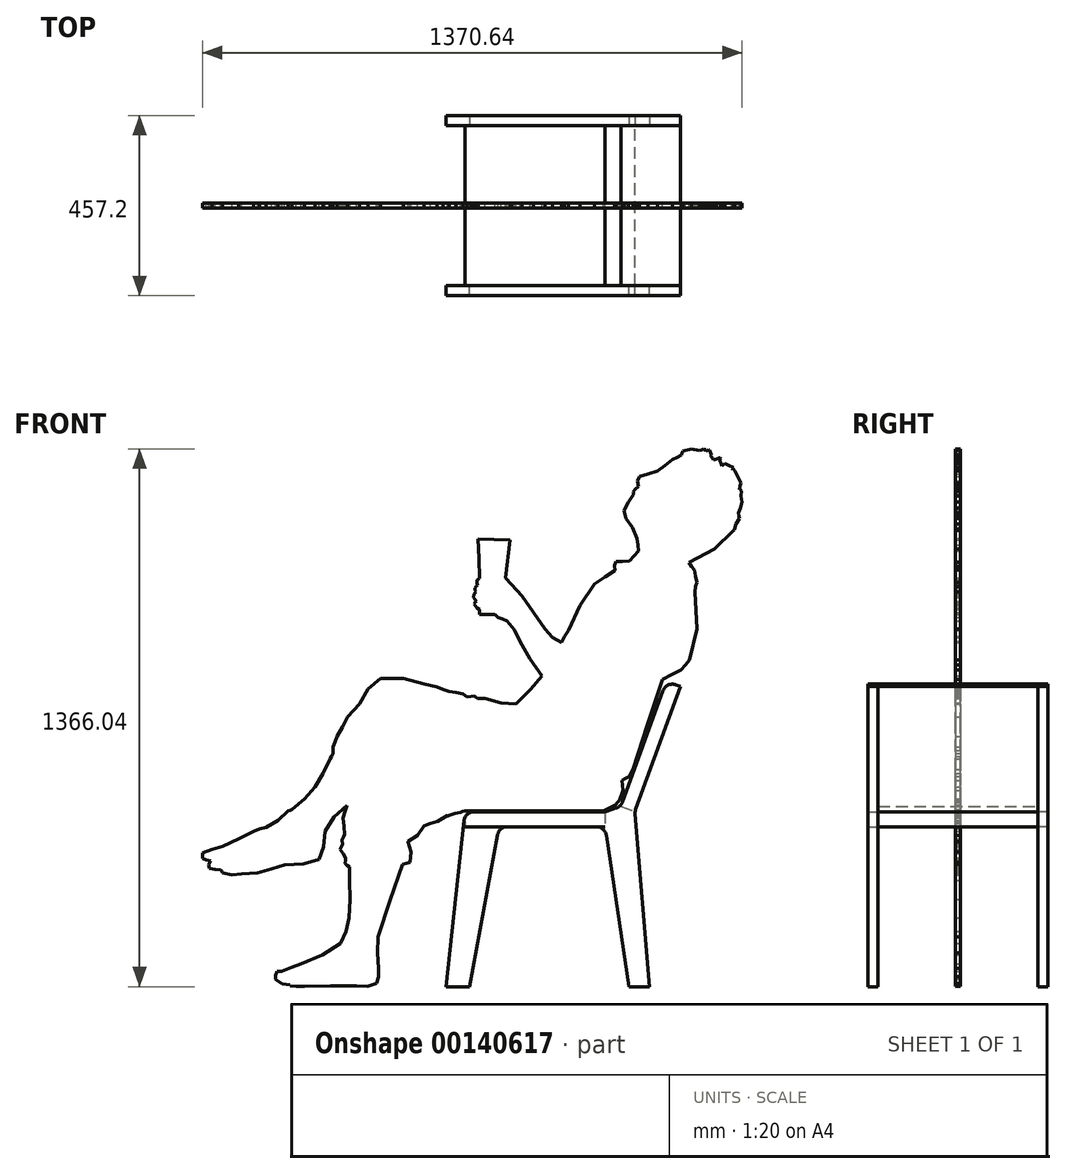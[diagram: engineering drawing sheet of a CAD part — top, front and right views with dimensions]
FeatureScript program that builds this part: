
annotation { "Feature Type Name" : "Feature", "Feature Type Description" : "" }
export const myFeature = defineFeature(function(context is Context, id is Id, definition is map)
    precondition{}
    {
        {
            var Q0;
            Q0=qCreatedBy(makeId("Front.planeOp"),FACE);
            var sketch = newSketch(context, id + "F0", { "sketchPlane" : qUnion([Q0])});
            skLineSegment(sketch, "E0", {"start": v(230.04, 462.13) * mm, "end": v(234.88, 467.85) * mm});
            skLineSegment(sketch, "E1", {"start": v(234.88, 467.85) * mm, "end": v(240.17, 473.23) * mm});
            skLineSegment(sketch, "E2", {"start": v(240.17, 473.23) * mm, "end": v(249.09, 499.16) * mm});
            skLineSegment(sketch, "E3", {"start": v(249.09, 499.16) * mm, "end": v(246.4, 524.65) * mm});
            skLineSegment(sketch, "E4", {"start": v(246.4, 524.65) * mm, "end": v(255.7, 529.38) * mm});
            skLineSegment(sketch, "E5", {"start": v(255.7, 529.38) * mm, "end": v(265.03, 534.12) * mm});
            skLineSegment(sketch, "E6", {"start": v(265.03, 534.12) * mm, "end": v(269.43, 542.97) * mm});
            skLineSegment(sketch, "E7", {"start": v(269.43, 542.97) * mm, "end": v(273.88, 551.78) * mm});
            skLineSegment(sketch, "E8", {"start": v(273.88, 551.78) * mm, "end": v(311.72, 666.33) * mm});
            skLineSegment(sketch, "E9", {"start": v(311.72, 666.33) * mm, "end": v(349.55, 780.89) * mm});
            skLineSegment(sketch, "E10", {"start": v(349.55, 780.89) * mm, "end": v(372.82, 793.09) * mm});
            skLineSegment(sketch, "E11", {"start": v(372.82, 793.09) * mm, "end": v(396.1, 805.28) * mm});
            skLineSegment(sketch, "E12", {"start": v(396.1, 805.28) * mm, "end": v(407.83, 817.46) * mm});
            skLineSegment(sketch, "E13", {"start": v(407.83, 817.46) * mm, "end": v(417.82, 830.69) * mm});
            skLineSegment(sketch, "E14", {"start": v(417.82, 830.69) * mm, "end": v(437.54, 908.46) * mm});
            skLineSegment(sketch, "E15", {"start": v(437.54, 908.46) * mm, "end": v(431.89, 1002.35) * mm});
            skLineSegment(sketch, "E16", {"start": v(431.89, 1002.35) * mm, "end": v(432.93, 1016.38) * mm});
            skLineSegment(sketch, "E17", {"start": v(432.93, 1016.38) * mm, "end": v(436.5, 1027.04) * mm});
            skLineSegment(sketch, "E18", {"start": v(436.5, 1027.04) * mm, "end": v(433.6, 1043) * mm});
            skLineSegment(sketch, "E19", {"start": v(433.6, 1043) * mm, "end": v(430.68, 1058.92) * mm});
            skLineSegment(sketch, "E20", {"start": v(430.68, 1058.92) * mm, "end": v(423.59, 1067.86) * mm});
            skLineSegment(sketch, "E21", {"start": v(423.59, 1067.86) * mm, "end": v(416.63, 1078.02) * mm});
            skLineSegment(sketch, "E22", {"start": v(416.63, 1078.02) * mm, "end": v(480.94, 1111.8) * mm});
            skLineSegment(sketch, "E23", {"start": v(480.94, 1111.8) * mm, "end": v(529.37, 1159.29) * mm});
            skLineSegment(sketch, "E24", {"start": v(529.37, 1159.29) * mm, "end": v(531.82, 1160.03) * mm});
            skLineSegment(sketch, "E25", {"start": v(531.82, 1160.03) * mm, "end": v(532.62, 1161.32) * mm});
            skLineSegment(sketch, "E26", {"start": v(532.62, 1161.32) * mm, "end": v(536.36, 1175.51) * mm});
            skLineSegment(sketch, "E27", {"start": v(536.36, 1175.51) * mm, "end": v(544.96, 1188.92) * mm});
            skLineSegment(sketch, "E28", {"start": v(544.96, 1188.92) * mm, "end": v(543.9, 1196.32) * mm});
            skLineSegment(sketch, "E29", {"start": v(543.9, 1196.32) * mm, "end": v(542.61, 1203.61) * mm});
            skLineSegment(sketch, "E30", {"start": v(542.61, 1203.61) * mm, "end": v(548.02, 1216.63) * mm});
            skLineSegment(sketch, "E31", {"start": v(548.02, 1216.63) * mm, "end": v(551.7, 1230.97) * mm});
            skLineSegment(sketch, "E32", {"start": v(551.7, 1230.97) * mm, "end": v(548.93, 1246.33) * mm});
            skLineSegment(sketch, "E33", {"start": v(548.93, 1246.33) * mm, "end": v(550.4, 1259.92) * mm});
            skLineSegment(sketch, "E34", {"start": v(550.4, 1259.92) * mm, "end": v(548.03, 1262.67) * mm});
            skLineSegment(sketch, "E35", {"start": v(548.03, 1262.67) * mm, "end": v(544.89, 1263.55) * mm});
            skLineSegment(sketch, "E36", {"start": v(544.89, 1263.55) * mm, "end": v(546.36, 1272.14) * mm});
            skLineSegment(sketch, "E37", {"start": v(546.36, 1272.14) * mm, "end": v(548.52, 1279.69) * mm});
            skLineSegment(sketch, "E38", {"start": v(548.52, 1279.69) * mm, "end": v(541.03, 1294.78) * mm});
            skLineSegment(sketch, "E39", {"start": v(541.03, 1294.78) * mm, "end": v(533.46, 1309.96) * mm});
            skLineSegment(sketch, "E40", {"start": v(533.46, 1309.96) * mm, "end": v(529.26, 1314.78) * mm});
            skLineSegment(sketch, "E41", {"start": v(529.26, 1314.78) * mm, "end": v(524.28, 1317.05) * mm});
            skLineSegment(sketch, "E42", {"start": v(524.28, 1317.05) * mm, "end": v(526.76, 1318) * mm});
            skLineSegment(sketch, "E43", {"start": v(526.76, 1318) * mm, "end": v(529.24, 1318.96) * mm});
            skLineSegment(sketch, "E44", {"start": v(529.24, 1318.96) * mm, "end": v(518.3, 1324.37) * mm});
            skLineSegment(sketch, "E45", {"start": v(518.3, 1324.37) * mm, "end": v(507.96, 1329.59) * mm});
            skLineSegment(sketch, "E46", {"start": v(507.96, 1329.59) * mm, "end": v(504.43, 1326.13) * mm});
            skLineSegment(sketch, "E47", {"start": v(504.43, 1326.13) * mm, "end": v(500.73, 1322.78) * mm});
            skLineSegment(sketch, "E48", {"start": v(500.73, 1322.78) * mm, "end": v(498.52, 1330.1) * mm});
            skLineSegment(sketch, "E49", {"start": v(498.52, 1330.1) * mm, "end": v(495.12, 1335.27) * mm});
            skLineSegment(sketch, "E50", {"start": v(495.12, 1335.27) * mm, "end": v(495.7, 1339.01) * mm});
            skLineSegment(sketch, "E51", {"start": v(495.7, 1339.01) * mm, "end": v(497.46, 1341.92) * mm});
            skLineSegment(sketch, "E52", {"start": v(497.46, 1341.92) * mm, "end": v(496.73, 1342.9) * mm});
            skLineSegment(sketch, "E53", {"start": v(496.73, 1342.9) * mm, "end": v(496.02, 1343.81) * mm});
            skLineSegment(sketch, "E54", {"start": v(496.02, 1343.81) * mm, "end": v(485.87, 1340.85) * mm});
            skLineSegment(sketch, "E55", {"start": v(485.87, 1340.85) * mm, "end": v(478.3, 1338.56) * mm});
            skLineSegment(sketch, "E56", {"start": v(478.3, 1338.56) * mm, "end": v(476.02, 1343.16) * mm});
            skLineSegment(sketch, "E57", {"start": v(476.02, 1343.16) * mm, "end": v(472.6, 1347.16) * mm});
            skLineSegment(sketch, "E58", {"start": v(472.6, 1347.16) * mm, "end": v(472.25, 1349.6) * mm});
            skLineSegment(sketch, "E59", {"start": v(472.25, 1349.6) * mm, "end": v(474.32, 1351.05) * mm});
            skLineSegment(sketch, "E60", {"start": v(474.32, 1351.05) * mm, "end": v(471.62, 1356.97) * mm});
            skLineSegment(sketch, "E61", {"start": v(471.62, 1356.97) * mm, "end": v(468.92, 1362.9) * mm});
            skLineSegment(sketch, "E62", {"start": v(468.92, 1362.9) * mm, "end": v(467.81, 1363.7) * mm});
            skLineSegment(sketch, "E63", {"start": v(467.81, 1363.7) * mm, "end": v(466.71, 1364.49) * mm});
            skLineSegment(sketch, "E64", {"start": v(466.71, 1364.49) * mm, "end": v(463.44, 1362.38) * mm});
            skLineSegment(sketch, "E65", {"start": v(463.44, 1362.38) * mm, "end": v(460.11, 1360.3) * mm});
            skLineSegment(sketch, "E66", {"start": v(460.11, 1360.3) * mm, "end": v(459.63, 1362.58) * mm});
            skLineSegment(sketch, "E67", {"start": v(459.63, 1362.58) * mm, "end": v(459.17, 1364.81) * mm});
            skLineSegment(sketch, "E68", {"start": v(459.17, 1364.81) * mm, "end": v(456.52, 1364.22) * mm});
            skLineSegment(sketch, "E69", {"start": v(456.52, 1364.22) * mm, "end": v(453.9, 1363.58) * mm});
            skLineSegment(sketch, "E70", {"start": v(453.9, 1363.58) * mm, "end": v(453.85, 1364.82) * mm});
            skLineSegment(sketch, "E71", {"start": v(453.85, 1364.82) * mm, "end": v(453.75, 1366.04) * mm});
            skLineSegment(sketch, "E72", {"start": v(453.75, 1366.04) * mm, "end": v(448.81, 1363.92) * mm});
            skLineSegment(sketch, "E73", {"start": v(448.81, 1363.92) * mm, "end": v(443.13, 1361.95) * mm});
            skLineSegment(sketch, "E74", {"start": v(443.13, 1361.95) * mm, "end": v(422.6, 1365.55) * mm});
            skLineSegment(sketch, "E75", {"start": v(422.6, 1365.55) * mm, "end": v(401.85, 1360.7) * mm});
            skLineSegment(sketch, "E76", {"start": v(401.85, 1360.7) * mm, "end": v(399.46, 1355.35) * mm});
            skLineSegment(sketch, "E77", {"start": v(399.46, 1355.35) * mm, "end": v(397.72, 1350.2) * mm});
            skLineSegment(sketch, "E78", {"start": v(397.72, 1350.2) * mm, "end": v(386.13, 1344.92) * mm});
            skLineSegment(sketch, "E79", {"start": v(386.13, 1344.92) * mm, "end": v(374.59, 1339.72) * mm});
            skLineSegment(sketch, "E80", {"start": v(374.59, 1339.72) * mm, "end": v(355.17, 1324.14) * mm});
            skLineSegment(sketch, "E81", {"start": v(355.17, 1324.14) * mm, "end": v(337.03, 1309.65) * mm});
            skLineSegment(sketch, "E82", {"start": v(337.03, 1309.65) * mm, "end": v(312.55, 1303.07) * mm});
            skLineSegment(sketch, "E83", {"start": v(312.55, 1303.07) * mm, "end": v(290.53, 1296.61) * mm});
            skLineSegment(sketch, "E84", {"start": v(290.53, 1296.61) * mm, "end": v(285.93, 1284.95) * mm});
            skLineSegment(sketch, "E85", {"start": v(285.93, 1284.95) * mm, "end": v(288.26, 1270.38) * mm});
            skLineSegment(sketch, "E86", {"start": v(288.26, 1270.38) * mm, "end": v(280.8, 1263.87) * mm});
            skLineSegment(sketch, "E87", {"start": v(280.8, 1263.87) * mm, "end": v(274.61, 1256.95) * mm});
            skLineSegment(sketch, "E88", {"start": v(274.61, 1256.95) * mm, "end": v(275.36, 1253.9) * mm});
            skLineSegment(sketch, "E89", {"start": v(275.36, 1253.9) * mm, "end": v(276.14, 1250.9) * mm});
            skLineSegment(sketch, "E90", {"start": v(276.14, 1250.9) * mm, "end": v(262.68, 1231.99) * mm});
            skLineSegment(sketch, "E91", {"start": v(262.68, 1231.99) * mm, "end": v(251.18, 1209.39) * mm});
            skLineSegment(sketch, "E92", {"start": v(251.18, 1209.39) * mm, "end": v(254.22, 1199.43) * mm});
            skLineSegment(sketch, "E93", {"start": v(254.22, 1199.43) * mm, "end": v(257.27, 1189.53) * mm});
            skLineSegment(sketch, "E94", {"start": v(257.27, 1189.53) * mm, "end": v(272.63, 1166.4) * mm});
            skLineSegment(sketch, "E95", {"start": v(272.63, 1166.4) * mm, "end": v(284.92, 1138.68) * mm});
            skLineSegment(sketch, "E96", {"start": v(284.92, 1138.68) * mm, "end": v(287.44, 1122) * mm});
            skLineSegment(sketch, "E97", {"start": v(287.44, 1122) * mm, "end": v(288.9, 1107.45) * mm});
            skLineSegment(sketch, "E98", {"start": v(288.9, 1107.45) * mm, "end": v(277.21, 1094.66) * mm});
            skLineSegment(sketch, "E99", {"start": v(277.21, 1094.66) * mm, "end": v(265.53, 1081.87) * mm});
            skLineSegment(sketch, "E100", {"start": v(265.53, 1081.87) * mm, "end": v(247.67, 1080.46) * mm});
            skLineSegment(sketch, "E101", {"start": v(247.67, 1080.46) * mm, "end": v(231.08, 1080.5) * mm});
            skLineSegment(sketch, "E102", {"start": v(231.08, 1080.5) * mm, "end": v(227.65, 1070.33) * mm});
            skLineSegment(sketch, "E103", {"start": v(227.65, 1070.33) * mm, "end": v(228.53, 1058.05) * mm});
            skLineSegment(sketch, "E104", {"start": v(228.53, 1058.05) * mm, "end": v(202.75, 1040.3) * mm});
            skLineSegment(sketch, "E105", {"start": v(202.75, 1040.3) * mm, "end": v(177.08, 1022.82) * mm});
            skLineSegment(sketch, "E106", {"start": v(177.08, 1022.82) * mm, "end": v(139.16, 968.13) * mm});
            skLineSegment(sketch, "E107", {"start": v(139.16, 968.13) * mm, "end": v(109.93, 904.75) * mm});
            skLineSegment(sketch, "E108", {"start": v(109.93, 904.75) * mm, "end": v(100.7, 890.27) * mm});
            skLineSegment(sketch, "E109", {"start": v(100.7, 890.27) * mm, "end": v(93.18, 874.2) * mm});
            skLineSegment(sketch, "E110", {"start": v(93.18, 874.2) * mm, "end": v(70, 887.69) * mm});
            skLineSegment(sketch, "E111", {"start": v(70, 887.69) * mm, "end": v(51.09, 908.58) * mm});
            skLineSegment(sketch, "E112", {"start": v(51.09, 908.58) * mm, "end": v(21.78, 950.3) * mm});
            skLineSegment(sketch, "E113", {"start": v(21.78, 950.3) * mm, "end": v(-7.05, 992.72) * mm});
            skLineSegment(sketch, "E114", {"start": v(-7.05, 992.72) * mm, "end": v(-33.86, 1021.5) * mm});
            skLineSegment(sketch, "E115", {"start": v(-33.86, 1021.5) * mm, "end": v(-49.2, 1038.65) * mm});
            skLineSegment(sketch, "E116", {"start": v(-49.2, 1038.65) * mm, "end": v(-43.72, 1086.56) * mm});
            skLineSegment(sketch, "E117", {"start": v(-43.72, 1086.56) * mm, "end": v(-38.25, 1134.46) * mm});
            skLineSegment(sketch, "E118", {"start": v(-38.25, 1134.46) * mm, "end": v(-78.7, 1135.95) * mm});
            skLineSegment(sketch, "E119", {"start": v(-78.7, 1135.95) * mm, "end": v(-119.17, 1137.43) * mm});
            skLineSegment(sketch, "E120", {"start": v(-119.17, 1137.43) * mm, "end": v(-117.11, 1087.39) * mm});
            skLineSegment(sketch, "E121", {"start": v(-117.11, 1087.39) * mm, "end": v(-115.06, 1037.35) * mm});
            skLineSegment(sketch, "E122", {"start": v(-115.06, 1037.35) * mm, "end": v(-117.64, 1035.89) * mm});
            skLineSegment(sketch, "E123", {"start": v(-117.64, 1035.89) * mm, "end": v(-121.98, 1033.53) * mm});
            skLineSegment(sketch, "E124", {"start": v(-121.98, 1033.53) * mm, "end": v(-122.11, 1025.82) * mm});
            skLineSegment(sketch, "E125", {"start": v(-122.11, 1025.82) * mm, "end": v(-120.34, 1018.98) * mm});
            skLineSegment(sketch, "E126", {"start": v(-120.34, 1018.98) * mm, "end": v(-124.37, 1016.55) * mm});
            skLineSegment(sketch, "E127", {"start": v(-124.37, 1016.55) * mm, "end": v(-127.26, 1012.88) * mm});
            skLineSegment(sketch, "E128", {"start": v(-127.26, 1012.88) * mm, "end": v(-126.4, 1007.04) * mm});
            skLineSegment(sketch, "E129", {"start": v(-126.4, 1007.04) * mm, "end": v(-124.25, 1002.96) * mm});
            skLineSegment(sketch, "E130", {"start": v(-124.25, 1002.96) * mm, "end": v(-129.38, 997.51) * mm});
            skLineSegment(sketch, "E131", {"start": v(-129.38, 997.51) * mm, "end": v(-131.14, 988.4) * mm});
            skLineSegment(sketch, "E132", {"start": v(-131.14, 988.4) * mm, "end": v(-127.32, 983.82) * mm});
            skLineSegment(sketch, "E133", {"start": v(-127.32, 983.82) * mm, "end": v(-123.5, 979.3) * mm});
            skLineSegment(sketch, "E134", {"start": v(-123.5, 979.3) * mm, "end": v(-126.91, 976.24) * mm});
            skLineSegment(sketch, "E135", {"start": v(-126.91, 976.24) * mm, "end": v(-129.6, 972.38) * mm});
            skLineSegment(sketch, "E136", {"start": v(-129.6, 972.38) * mm, "end": v(-121.4, 962.6) * mm});
            skLineSegment(sketch, "E137", {"start": v(-121.4, 962.6) * mm, "end": v(-115.88, 958.57) * mm});
            skLineSegment(sketch, "E138", {"start": v(-115.88, 958.57) * mm, "end": v(-115.52, 951.93) * mm});
            skLineSegment(sketch, "E139", {"start": v(-115.52, 951.93) * mm, "end": v(-115.17, 945.28) * mm});
            skLineSegment(sketch, "E140", {"start": v(-115.17, 945.28) * mm, "end": v(-95.87, 945.27) * mm});
            skLineSegment(sketch, "E141", {"start": v(-95.87, 945.27) * mm, "end": v(-76.58, 945.26) * mm});
            skLineSegment(sketch, "E142", {"start": v(-76.58, 945.26) * mm, "end": v(-73.71, 942.66) * mm});
            skLineSegment(sketch, "E143", {"start": v(-73.71, 942.66) * mm, "end": v(-68.94, 938.35) * mm});
            skLineSegment(sketch, "E144", {"start": v(-68.94, 938.35) * mm, "end": v(-57.08, 933.8) * mm});
            skLineSegment(sketch, "E145", {"start": v(-57.08, 933.8) * mm, "end": v(-45.27, 929.22) * mm});
            skLineSegment(sketch, "E146", {"start": v(-45.27, 929.22) * mm, "end": v(-26, 906.15) * mm});
            skLineSegment(sketch, "E147", {"start": v(-26, 906.15) * mm, "end": v(-12.33, 877.2) * mm});
            skLineSegment(sketch, "E148", {"start": v(-12.33, 877.2) * mm, "end": v(13.03, 832.18) * mm});
            skLineSegment(sketch, "E149", {"start": v(13.03, 832.18) * mm, "end": v(43.42, 790.04) * mm});
            skLineSegment(sketch, "E150", {"start": v(43.42, 790.04) * mm, "end": v(13.9, 755.16) * mm});
            skLineSegment(sketch, "E151", {"start": v(13.9, 755.16) * mm, "end": v(-22.35, 718.16) * mm});
            skLineSegment(sketch, "E152", {"start": v(-22.35, 718.16) * mm, "end": v(-60.27, 721.38) * mm});
            skLineSegment(sketch, "E153", {"start": v(-60.27, 721.38) * mm, "end": v(-100.99, 731.9) * mm});
            skLineSegment(sketch, "E154", {"start": v(-100.99, 731.9) * mm, "end": v(-110.57, 731.9) * mm});
            skLineSegment(sketch, "E155", {"start": v(-110.57, 731.9) * mm, "end": v(-120.16, 731.9) * mm});
            skLineSegment(sketch, "E156", {"start": v(-120.16, 731.9) * mm, "end": v(-124.31, 735.02) * mm});
            skLineSegment(sketch, "E157", {"start": v(-124.31, 735.02) * mm, "end": v(-128.53, 738.14) * mm});
            skLineSegment(sketch, "E158", {"start": v(-128.53, 738.14) * mm, "end": v(-137.47, 736.93) * mm});
            skLineSegment(sketch, "E159", {"start": v(-137.47, 736.93) * mm, "end": v(-146.84, 736.53) * mm});
            skLineSegment(sketch, "E160", {"start": v(-146.84, 736.53) * mm, "end": v(-151.88, 740) * mm});
            skLineSegment(sketch, "E161", {"start": v(-151.88, 740) * mm, "end": v(-156.9, 743.44) * mm});
            skLineSegment(sketch, "E162", {"start": v(-156.9, 743.44) * mm, "end": v(-175.45, 747.74) * mm});
            skLineSegment(sketch, "E163", {"start": v(-175.45, 747.74) * mm, "end": v(-192.85, 749.54) * mm});
            skLineSegment(sketch, "E164", {"start": v(-192.85, 749.54) * mm, "end": v(-208.38, 755.07) * mm});
            skLineSegment(sketch, "E165", {"start": v(-208.38, 755.07) * mm, "end": v(-223.4, 761.75) * mm});
            skLineSegment(sketch, "E166", {"start": v(-223.4, 761.75) * mm, "end": v(-239.82, 765.23) * mm});
            skLineSegment(sketch, "E167", {"start": v(-239.82, 765.23) * mm, "end": v(-256.27, 768.7) * mm});
            skLineSegment(sketch, "E168", {"start": v(-256.27, 768.7) * mm, "end": v(-307.93, 783.23) * mm});
            skLineSegment(sketch, "E169", {"start": v(-307.93, 783.23) * mm, "end": v(-367.1, 783.27) * mm});
            skLineSegment(sketch, "E170", {"start": v(-367.1, 783.27) * mm, "end": v(-399.17, 756.72) * mm});
            skLineSegment(sketch, "E171", {"start": v(-399.17, 756.72) * mm, "end": v(-419.88, 718.96) * mm});
            skLineSegment(sketch, "E172", {"start": v(-419.88, 718.96) * mm, "end": v(-435.28, 702.03) * mm});
            skLineSegment(sketch, "E173", {"start": v(-435.28, 702.03) * mm, "end": v(-450.44, 685.3) * mm});
            skLineSegment(sketch, "E174", {"start": v(-450.44, 685.3) * mm, "end": v(-463.78, 660.52) * mm});
            skLineSegment(sketch, "E175", {"start": v(-463.78, 660.52) * mm, "end": v(-477.12, 635.7) * mm});
            skLineSegment(sketch, "E176", {"start": v(-477.12, 635.7) * mm, "end": v(-482.52, 622.23) * mm});
            skLineSegment(sketch, "E177", {"start": v(-482.52, 622.23) * mm, "end": v(-487.92, 608.87) * mm});
            skLineSegment(sketch, "E178", {"start": v(-487.92, 608.87) * mm, "end": v(-487.47, 600.5) * mm});
            skLineSegment(sketch, "E179", {"start": v(-487.47, 600.5) * mm, "end": v(-487.1, 592.05) * mm});
            skLineSegment(sketch, "E180", {"start": v(-487.1, 592.05) * mm, "end": v(-491.3, 585.12) * mm});
            skLineSegment(sketch, "E181", {"start": v(-491.3, 585.12) * mm, "end": v(-495.55, 578.3) * mm});
            skLineSegment(sketch, "E182", {"start": v(-495.55, 578.3) * mm, "end": v(-513.41, 541.7) * mm});
            skLineSegment(sketch, "E183", {"start": v(-513.41, 541.7) * mm, "end": v(-533.77, 507.15) * mm});
            skLineSegment(sketch, "E184", {"start": v(-533.77, 507.15) * mm, "end": v(-560.32, 476.63) * mm});
            skLineSegment(sketch, "E185", {"start": v(-560.32, 476.63) * mm, "end": v(-591.8, 450.63) * mm});
            skLineSegment(sketch, "E186", {"start": v(-591.8, 450.63) * mm, "end": v(-596.83, 448.3) * mm});
            skLineSegment(sketch, "E187", {"start": v(-596.83, 448.3) * mm, "end": v(-601.77, 446.02) * mm});
            skLineSegment(sketch, "E188", {"start": v(-601.77, 446.02) * mm, "end": v(-627.48, 422.78) * mm});
            skLineSegment(sketch, "E189", {"start": v(-627.48, 422.78) * mm, "end": v(-657.56, 404.78) * mm});
            skLineSegment(sketch, "E190", {"start": v(-657.56, 404.78) * mm, "end": v(-673.7, 400.57) * mm});
            skLineSegment(sketch, "E191", {"start": v(-673.7, 400.57) * mm, "end": v(-689.72, 394.84) * mm});
            skLineSegment(sketch, "E192", {"start": v(-689.72, 394.84) * mm, "end": v(-727.66, 374.82) * mm});
            skLineSegment(sketch, "E193", {"start": v(-727.66, 374.82) * mm, "end": v(-768.44, 356.56) * mm});
            skLineSegment(sketch, "E194", {"start": v(-768.44, 356.56) * mm, "end": v(-794.43, 348.33) * mm});
            skLineSegment(sketch, "E195", {"start": v(-794.43, 348.33) * mm, "end": v(-818.95, 339.74) * mm});
            skLineSegment(sketch, "E196", {"start": v(-818.95, 339.74) * mm, "end": v(-818.95, 332.86) * mm});
            skLineSegment(sketch, "E197", {"start": v(-818.95, 332.86) * mm, "end": v(-818.95, 325.99) * mm});
            skLineSegment(sketch, "E198", {"start": v(-818.95, 325.99) * mm, "end": v(-810.31, 321.5) * mm});
            skLineSegment(sketch, "E199", {"start": v(-810.31, 321.5) * mm, "end": v(-799.03, 319.16) * mm});
            skLineSegment(sketch, "E200", {"start": v(-799.03, 319.16) * mm, "end": v(-804.36, 309.45) * mm});
            skLineSegment(sketch, "E201", {"start": v(-804.36, 309.45) * mm, "end": v(-801.23, 300.05) * mm});
            skLineSegment(sketch, "E202", {"start": v(-801.23, 300.05) * mm, "end": v(-787.66, 297.4) * mm});
            skLineSegment(sketch, "E203", {"start": v(-787.66, 297.4) * mm, "end": v(-773.1, 296.15) * mm});
            skLineSegment(sketch, "E204", {"start": v(-773.1, 296.15) * mm, "end": v(-769.98, 292.51) * mm});
            skLineSegment(sketch, "E205", {"start": v(-769.98, 292.51) * mm, "end": v(-767.66, 288.59) * mm});
            skLineSegment(sketch, "E206", {"start": v(-767.66, 288.59) * mm, "end": v(-744.6, 283.58) * mm});
            skLineSegment(sketch, "E207", {"start": v(-744.6, 283.58) * mm, "end": v(-720.31, 286.24) * mm});
            skLineSegment(sketch, "E208", {"start": v(-720.31, 286.24) * mm, "end": v(-699.62, 287.81) * mm});
            skLineSegment(sketch, "E209", {"start": v(-699.62, 287.81) * mm, "end": v(-678.92, 289.39) * mm});
            skLineSegment(sketch, "E210", {"start": v(-678.92, 289.39) * mm, "end": v(-644.43, 299.2) * mm});
            skLineSegment(sketch, "E211", {"start": v(-644.43, 299.2) * mm, "end": v(-610.96, 309.16) * mm});
            skLineSegment(sketch, "E212", {"start": v(-610.96, 309.16) * mm, "end": v(-562.45, 312.04) * mm});
            skLineSegment(sketch, "E213", {"start": v(-562.45, 312.04) * mm, "end": v(-522.98, 322.98) * mm});
            skLineSegment(sketch, "E214", {"start": v(-522.98, 322.98) * mm, "end": v(-512.12, 354.89) * mm});
            skLineSegment(sketch, "E215", {"start": v(-512.12, 354.89) * mm, "end": v(-508.42, 394.84) * mm});
            skLineSegment(sketch, "E216", {"start": v(-508.42, 394.84) * mm, "end": v(-484.5, 431.35) * mm});
            skLineSegment(sketch, "E217", {"start": v(-484.5, 431.35) * mm, "end": v(-451.93, 460.55) * mm});
            skLineSegment(sketch, "E218", {"start": v(-451.93, 460.55) * mm, "end": v(-456.9, 444.92) * mm});
            skLineSegment(sketch, "E219", {"start": v(-456.9, 444.92) * mm, "end": v(-461.83, 429.18) * mm});
            skLineSegment(sketch, "E220", {"start": v(-461.83, 429.18) * mm, "end": v(-460.08, 406.95) * mm});
            skLineSegment(sketch, "E221", {"start": v(-460.08, 406.95) * mm, "end": v(-458.07, 387.14) * mm});
            skLineSegment(sketch, "E222", {"start": v(-458.07, 387.14) * mm, "end": v(-461.08, 379.92) * mm});
            skLineSegment(sketch, "E223", {"start": v(-461.08, 379.92) * mm, "end": v(-464.17, 372.58) * mm});
            skLineSegment(sketch, "E224", {"start": v(-464.17, 372.58) * mm, "end": v(-463.08, 362) * mm});
            skLineSegment(sketch, "E225", {"start": v(-463.08, 362) * mm, "end": v(-470.24, 349) * mm});
            skLineSegment(sketch, "E226", {"start": v(-470.24, 349) * mm, "end": v(-462.35, 338.23) * mm});
            skLineSegment(sketch, "E227", {"start": v(-462.35, 338.23) * mm, "end": v(-455.72, 327.48) * mm});
            skLineSegment(sketch, "E228", {"start": v(-455.72, 327.48) * mm, "end": v(-456.16, 320.29) * mm});
            skLineSegment(sketch, "E229", {"start": v(-456.16, 320.29) * mm, "end": v(-457.37, 313.06) * mm});
            skLineSegment(sketch, "E230", {"start": v(-457.37, 313.06) * mm, "end": v(-451.58, 308.4) * mm});
            skLineSegment(sketch, "E231", {"start": v(-451.58, 308.4) * mm, "end": v(-445.83, 303.86) * mm});
            skLineSegment(sketch, "E232", {"start": v(-445.83, 303.86) * mm, "end": v(-445.83, 286.67) * mm});
            skLineSegment(sketch, "E233", {"start": v(-445.83, 286.67) * mm, "end": v(-445.83, 269.47) * mm});
            skLineSegment(sketch, "E234", {"start": v(-445.83, 269.47) * mm, "end": v(-444.19, 221.53) * mm});
            skLineSegment(sketch, "E235", {"start": v(-444.19, 221.53) * mm, "end": v(-447.27, 175.4) * mm});
            skLineSegment(sketch, "E236", {"start": v(-447.27, 175.4) * mm, "end": v(-455.13, 140.65) * mm});
            skLineSegment(sketch, "E237", {"start": v(-455.13, 140.65) * mm, "end": v(-468, 110.43) * mm});
            skLineSegment(sketch, "E238", {"start": v(-468, 110.43) * mm, "end": v(-514, 81.15) * mm});
            skLineSegment(sketch, "E239", {"start": v(-514, 81.15) * mm, "end": v(-568.99, 58.48) * mm});
            skLineSegment(sketch, "E240", {"start": v(-568.99, 58.48) * mm, "end": v(-593.37, 48.93) * mm});
            skLineSegment(sketch, "E241", {"start": v(-593.37, 48.93) * mm, "end": v(-617.8, 39.29) * mm});
            skLineSegment(sketch, "E242", {"start": v(-617.8, 39.29) * mm, "end": v(-623.97, 39.29) * mm});
            skLineSegment(sketch, "E243", {"start": v(-623.97, 39.29) * mm, "end": v(-630.14, 39.29) * mm});
            skLineSegment(sketch, "E244", {"start": v(-630.14, 39.29) * mm, "end": v(-633.72, 29.1) * mm});
            skLineSegment(sketch, "E245", {"start": v(-633.72, 29.1) * mm, "end": v(-633.07, 17.96) * mm});
            skLineSegment(sketch, "E246", {"start": v(-633.07, 17.96) * mm, "end": v(-616.71, 7.63) * mm});
            skLineSegment(sketch, "E247", {"start": v(-616.71, 7.63) * mm, "end": v(-597.16, 4.23) * mm});
            skLineSegment(sketch, "E248", {"start": v(-597.16, 4.23) * mm, "end": v(-597.16, 3.06) * mm});
            skLineSegment(sketch, "E249", {"start": v(-597.16, 3.06) * mm, "end": v(-597.16, 1.88) * mm});
            skLineSegment(sketch, "E250", {"start": v(-597.16, 1.88) * mm, "end": v(-581.37, 0.93) * mm});
            skLineSegment(sketch, "E251", {"start": v(-581.37, 0.93) * mm, "end": v(-560.46, 1.08) * mm});
            skLineSegment(sketch, "E252", {"start": v(-560.46, 1.08) * mm, "end": v(-494.28, 1.43) * mm});
            skLineSegment(sketch, "E253", {"start": v(-494.28, 1.43) * mm, "end": v(-428.26, 1.88) * mm});
            skLineSegment(sketch, "E254", {"start": v(-428.26, 1.88) * mm, "end": v(-399.84, 0.86) * mm});
            skLineSegment(sketch, "E255", {"start": v(-399.84, 0.86) * mm, "end": v(-377, 7.99) * mm});
            skLineSegment(sketch, "E256", {"start": v(-377, 7.99) * mm, "end": v(-371.6, 24.52) * mm});
            skLineSegment(sketch, "E257", {"start": v(-371.6, 24.52) * mm, "end": v(-371.65, 46.2) * mm});
            skLineSegment(sketch, "E258", {"start": v(-371.65, 46.2) * mm, "end": v(-374.96, 85.69) * mm});
            skLineSegment(sketch, "E259", {"start": v(-374.96, 85.69) * mm, "end": v(-373.95, 126.53) * mm});
            skLineSegment(sketch, "E260", {"start": v(-373.95, 126.53) * mm, "end": v(-342.83, 219.17) * mm});
            skLineSegment(sketch, "E261", {"start": v(-342.83, 219.17) * mm, "end": v(-311.24, 310.7) * mm});
            skLineSegment(sketch, "E262", {"start": v(-311.24, 310.7) * mm, "end": v(-301.71, 313.42) * mm});
            skLineSegment(sketch, "E263", {"start": v(-301.71, 313.42) * mm, "end": v(-292.07, 316.07) * mm});
            skLineSegment(sketch, "E264", {"start": v(-292.07, 316.07) * mm, "end": v(-289.92, 342) * mm});
            skLineSegment(sketch, "E265", {"start": v(-289.92, 342) * mm, "end": v(-297.5, 367.3) * mm});
            skLineSegment(sketch, "E266", {"start": v(-297.5, 367.3) * mm, "end": v(-297.5, 368.44) * mm});
            skLineSegment(sketch, "E267", {"start": v(-297.5, 368.44) * mm, "end": v(-297.5, 369.57) * mm});
            skLineSegment(sketch, "E268", {"start": v(-297.5, 369.57) * mm, "end": v(-273.06, 384.8) * mm});
            skLineSegment(sketch, "E269", {"start": v(-273.06, 384.8) * mm, "end": v(-257.01, 408.65) * mm});
            skLineSegment(sketch, "E270", {"start": v(-257.01, 408.65) * mm, "end": v(-240.44, 414.5) * mm});
            skLineSegment(sketch, "E271", {"start": v(-240.44, 414.5) * mm, "end": v(-222.54, 419.32) * mm});
            skLineSegment(sketch, "E272", {"start": v(-222.54, 419.32) * mm, "end": v(-209.98, 426.97) * mm});
            skLineSegment(sketch, "E273", {"start": v(-209.98, 426.97) * mm, "end": v(-197.35, 434.61) * mm});
            skLineSegment(sketch, "E274", {"start": v(-197.35, 434.61) * mm, "end": v(-196.3, 434.31) * mm});
            skLineSegment(sketch, "E275", {"start": v(-196.3, 434.31) * mm, "end": v(-195.24, 434.06) * mm});
            skLineSegment(sketch, "E276", {"start": v(-195.24, 434.06) * mm, "end": v(-192.57, 435.13) * mm});
            skLineSegment(sketch, "E277", {"start": v(-192.57, 435.13) * mm, "end": v(-189.8, 436.08) * mm});
            skLineSegment(sketch, "E278", {"start": v(-189.8, 436.08) * mm, "end": v(-178.04, 440.67) * mm});
            skLineSegment(sketch, "E279", {"start": v(-178.04, 440.67) * mm, "end": v(-164.4, 442.8) * mm});
            skLineSegment(sketch, "E280", {"start": v(-164.4, 442.8) * mm, "end": v(-158.51, 445.27) * mm});
            skLineSegment(sketch, "E281", {"start": v(-158.51, 445.27) * mm, "end": v(-152.24, 446.6) * mm});
            skLineSegment(sketch, "E282", {"start": v(-152.24, 446.6) * mm, "end": v(-152.25, 446.65) * mm});
            skLineSegment(sketch, "E283", {"start": v(-152.25, 446.65) * mm, "end": v(-152.26, 446.71) * mm});
            skLineSegment(sketch, "E284", {"start": v(-152.26, 446.71) * mm, "end": v(-151.55, 446.71) * mm});
            skLineSegment(sketch, "E285", {"start": v(-151.55, 446.71) * mm, "end": v(-150.85, 446.71) * mm});
            skLineSegment(sketch, "E286", {"start": v(-150.85, 446.71) * mm, "end": v(-146.18, 446.86) * mm});
            skLineSegment(sketch, "E287", {"start": v(-146.18, 446.86) * mm, "end": v(-141.07, 446.72) * mm});
            skLineSegment(sketch, "E288", {"start": v(-141.07, 446.72) * mm, "end": v(29.3, 446.85) * mm});
            skLineSegment(sketch, "E289", {"start": v(29.3, 446.85) * mm, "end": v(199.68, 446.99) * mm});
            skLineSegment(sketch, "E290", {"start": v(199.68, 446.99) * mm, "end": v(214.86, 454.56) * mm});
            skLineSegment(sketch, "E291", {"start": v(214.86, 454.56) * mm, "end": v(230.04, 462.13) * mm});
            skSolve(sketch);
        }
        {
            var Q0;
            Q0=qSketchRegion(id+"F0",true);
            extrude(context, id + "F1", {"entities" : qUnion([Q0]), "depth" : 6.35 * mm, "hasSecondDirection" : true, "secondDirectionOppositeDirection" : true, "secondDirectionDepth" : 6.35 * mm});
        }
        {
            var Q0;
            Q0=qCreatedBy(makeId("Front.planeOp"),FACE);
            var sketch = newSketch(context, id + "F2", { "sketchPlane" : qUnion([Q0])});
            skLineSegment(sketch, "E292.bottom", {"start": v(-152.4, 444.5) * mm, "end": v(203.2, 444.5) * mm});
            skLineSegment(sketch, "E292.top", {"start": v(-152.4, 406.4) * mm, "end": v(203.2, 406.4) * mm});
            skLineSegment(sketch, "E292.left", {"start": v(-152.4, 444.5) * mm, "end": v(-152.4, 406.4) * mm});
            skLineSegment(sketch, "E292.right", {"start": v(203.2, 444.5) * mm, "end": v(203.2, 406.4) * mm});
            skLineSegment(sketch, "E293", {"start": v(-152.4, 406.4) * mm, "end": v(-152.4, 0) * mm, "construction": true});
            skLineSegment(sketch, "E294", {"start": v(-152.4, 0) * mm, "end": v(203.2, 0) * mm, "construction": true});
            skLineSegment(sketch, "E295", {"start": v(203.2, 0) * mm, "end": v(203.2, 406.4) * mm, "construction": true});
            skLineSegment(sketch, "E296", {"start": v(359.48, 775.9) * mm, "end": v(243.6, 457.53) * mm});
            skLineSegment(sketch, "E297", {"start": v(243.6, 457.53) * mm, "end": v(279.4, 444.5) * mm});
            skLineSegment(sketch, "E298", {"start": v(279.4, 444.5) * mm, "end": v(395.28, 762.87) * mm});
            skLineSegment(sketch, "E299", {"start": v(395.28, 762.87) * mm, "end": v(359.48, 775.9) * mm});
            skLineSegment(sketch, "E300", {"start": v(203.2, 444.5) * mm, "end": v(279.4, 444.5) * mm, "construction": true});
            skSolve(sketch);
        }
        {
            var Q0;
            Q0 = qSketchRegion(id + "F2", true);
            extrude(context, id + "F3", {"entities" : qUnion([Q0]), "depth" : 203.2 * mm, "hasSecondDirection" : true, "secondDirectionOppositeDirection" : true, "secondDirectionDepth" : 203.2 * mm});
        }
        {
            var Q0;
            Q0=makeQuery(id+"F3.opExtrude","CAP_FACE",FACE,{"disambiguationData":[OSD([sQuery(id+"F2.wireOp",EDGE,"E292.bottom"),sQuery(id+"F2.wireOp",EDGE,"E292.top"),sQuery(id+"F2.wireOp",EDGE,"E292.left"),sQuery(id+"F2.wireOp",EDGE,"E292.right")])],"isStart":false});
            cPlane(context, id + "F4", {"entities" : qUnion([Q0]), "cplaneType" : CPlaneType.OFFSET, "offset" : 0 * mm, "width" : 152.4 * mm, "height" : 152.4 * mm});
        }
        {
            var Q0;
            Q0=qCreatedBy(id+"F4.planeOp",FACE);
            var sketch = newSketch(context, id + "F5", { "sketchPlane" : qUnion([Q0])});
            skLineSegment(sketch, "E301.0", {"start": v(279.4, 444.5) * mm, "end": v(395.28, 762.87) * mm});
            skLineSegment(sketch, "E302.0.0", {"start": v(395.28, 762.87) * mm, "end": v(359.48, 775.9) * mm});
            skLineSegment(sketch, "E302.0.1", {"start": v(359.48, 775.9) * mm, "end": v(243.6, 457.53) * mm});
            skLineSegment(sketch, "E303.0.0", {"start": v(203.2, 444.5) * mm, "end": v(-152.4, 444.5) * mm});
            skLineSegment(sketch, "E304", {"start": v(279.4, 444.5) * mm, "end": v(316.34, 0) * mm});
            skLineSegment(sketch, "E305", {"start": v(316.34, 0) * mm, "end": v(264.09, 0) * mm});
            skLineSegment(sketch, "E306", {"start": v(264.09, 0) * mm, "end": v(203.2, 406.4) * mm});
            skLineSegment(sketch, "E307", {"start": v(203.2, 406.4) * mm, "end": v(-66.1, 406.4) * mm});
            skLineSegment(sketch, "E308", {"start": v(-66.1, 406.4) * mm, "end": v(-140.75, 0) * mm});
            skLineSegment(sketch, "E309", {"start": v(-140.75, 0) * mm, "end": v(-201.23, 0) * mm});
            skLineSegment(sketch, "E310", {"start": v(-201.23, 0) * mm, "end": v(-152.4, 444.5) * mm});
            skLineSegment(sketch, "E311", {"start": v(203.2, 444.5) * mm, "end": v(243.6, 457.53) * mm});
            skSolve(sketch);
        }
        {
            var Q0;
            Q0=makeQuery(id+"F5.imprint","IMPRINT",FACE,{"disambiguationData":[TD([[makeQuery(id+"F5.imprint","IMPRINT",EDGE,{"derivedFrom":sQuery(id+"F5.wireOp",EDGE,"E303.0.0")}),-1.0]])]});
            var Q1;
            {var subQ2=sQuery(id+"F5.wireOp",EDGE,"E308");Q1=makeQuery(id+"F5.imprint","IMPRINT",FACE,{"disambiguationData":[TD([[makeQuery(id+"F5.imprint","IMPRINT",EDGE,{"derivedFrom":subQ2}),-1.0]])]});}
            var Q2;
            Q2=makeQuery(id+"F5.imprint","IMPRINT",FACE,{"disambiguationData":[TD([[makeQuery(id+"F5.imprint","IMPRINT",EDGE,{"derivedFrom":sQuery(id+"F5.wireOp",EDGE,"E302.0.0")}),1.0]])]});
            extrude(context, id + "F6", {"entities" : qUnion([Q0, Q1, Q2]), "depth" : 25.4 * mm});
        }
        {
            var Q0;
            Q0=makeQuery(id+"F3.opExtrude","SWEPT_EDGE",EDGE,{"disambiguationData":[OSD([sQuery(id+"F2.wireOp",EDGE,"E292.bottom"),sQuery(id+"F2.wireOp",EDGE,"E292.left")])]});
            var Q1;
            Q1=makeQuery(id+"F8.opPattern","COPY",EDGE,{"derivedFrom":makeQuery(id+"F6.opExtrude","SWEPT_EDGE",EDGE,{"disambiguationData":[OSD([sQuery(id+"F5.wireOp",EDGE,"E303.0.0"),sQuery(id+"F5.wireOp",EDGE,"E310")])]}),"instanceName":"1"});
            var Q2;
            Q2=makeQuery(id+"F6.opExtrude","SWEPT_EDGE",EDGE,{"disambiguationData":[OSD([sQuery(id+"F5.wireOp",EDGE,"E303.0.0"),sQuery(id+"F5.wireOp",EDGE,"E310")])]});
            var Q3;
            Q3=makeQuery(id+"F6.opExtrude","SWEPT_EDGE",EDGE,{"disambiguationData":[OSD([sQuery(id+"F5.wireOp",EDGE,"E302.0.0"),sQuery(id+"F5.wireOp",EDGE,"E302.0.1")])]});
            var Q4;
            Q4=makeQuery(id+"F3.opExtrude","SWEPT_EDGE",EDGE,{"disambiguationData":[OSD([sQuery(id+"F2.wireOp",EDGE,"E296"),sQuery(id+"F2.wireOp",EDGE,"E299")])]});
            var Q5;
            Q5=makeQuery(id+"F8.opPattern","COPY",EDGE,{"derivedFrom":makeQuery(id+"F6.opExtrude","SWEPT_EDGE",EDGE,{"disambiguationData":[OSD([sQuery(id+"F5.wireOp",EDGE,"E302.0.0"),sQuery(id+"F5.wireOp",EDGE,"E302.0.1")])]}),"instanceName":"1"});
            var Q6;
            Q6=makeQuery(id+"F6.opExtrude","SWEPT_EDGE",EDGE,{"disambiguationData":[OSD([sQuery(id+"F5.wireOp",EDGE,"E303.0.0"),sQuery(id+"F5.wireOp",EDGE,"E311")])]});
            var Q7;
            Q7=makeQuery(id+"F6.opExtrude","SWEPT_EDGE",EDGE,{"disambiguationData":[OSD([sQuery(id+"F5.wireOp",EDGE,"E302.0.1"),sQuery(id+"F5.wireOp",EDGE,"E311")])]});
            var Q8;
            Q8=makeQuery(id+"F8.opPattern","COPY",EDGE,{"derivedFrom":makeQuery(id+"F6.opExtrude","SWEPT_EDGE",EDGE,{"disambiguationData":[OSD([sQuery(id+"F5.wireOp",EDGE,"E303.0.0"),sQuery(id+"F5.wireOp",EDGE,"E311")])]}),"instanceName":"1"});
            var Q9;
            Q9=makeQuery(id+"F8.opPattern","COPY",EDGE,{"derivedFrom":makeQuery(id+"F6.opExtrude","SWEPT_EDGE",EDGE,{"disambiguationData":[OSD([sQuery(id+"F5.wireOp",EDGE,"E302.0.1"),sQuery(id+"F5.wireOp",EDGE,"E311")])]}),"instanceName":"1"});
            var Q10;
            Q10=makeQuery(id+"F6.opExtrude","SWEPT_EDGE",EDGE,{"disambiguationData":[OSD([sQuery(id+"F5.wireOp",EDGE,"E301.0"),sQuery(id+"F5.wireOp",EDGE,"E304")])]});
            var Q11;
            Q11=makeQuery(id+"F8.opPattern","COPY",EDGE,{"derivedFrom":makeQuery(id+"F6.opExtrude","SWEPT_EDGE",EDGE,{"disambiguationData":[OSD([sQuery(id+"F5.wireOp",EDGE,"E301.0"),sQuery(id+"F5.wireOp",EDGE,"E304")])]}),"instanceName":"1"});
            var Q12;
            Q12=makeQuery(id+"F6.opExtrude","SWEPT_EDGE",EDGE,{"disambiguationData":[OSD([sQuery(id+"F5.wireOp",EDGE,"E306"),sQuery(id+"F5.wireOp",EDGE,"E307")])]});
            var Q13;
            Q13=makeQuery(id+"F6.opExtrude","SWEPT_EDGE",EDGE,{"disambiguationData":[OSD([sQuery(id+"F5.wireOp",EDGE,"E307"),sQuery(id+"F5.wireOp",EDGE,"E308")])]});
            fillet(context, id + "F7", {"entities" : qUnion([Q0, Q1, Q2, Q3, Q4, Q5, Q6, Q7, Q8, Q9, Q10, Q11, Q12, Q13]), "radius" : 25.4 * mm, "tangentPropagation" : true, "allowEdgeOverflow" : false});
        }
        {
            var Q0;
            Q0=makeQuery(id+"F6.opExtrude","SWEPT_BODY",BODY,{"disambiguationData":[OSD([sQuery(id+"F5.wireOp",EDGE,"E302.0.0"),sQuery(id+"F5.wireOp",EDGE,"E302.0.1"),sQuery(id+"F5.wireOp",EDGE,"E301.0"),sQuery(id+"F5.wireOp",EDGE,"E303.0.0"),sQuery(id+"F5.wireOp",EDGE,"E304"),sQuery(id+"F5.wireOp",EDGE,"E305"),sQuery(id+"F5.wireOp",EDGE,"E306"),sQuery(id+"F5.wireOp",EDGE,"E307"),sQuery(id+"F5.wireOp",EDGE,"E308"),sQuery(id+"F5.wireOp",EDGE,"E309"),sQuery(id+"F5.wireOp",EDGE,"E310"),sQuery(id+"F5.wireOp",EDGE,"E311")])]});
            var Q1;
            Q1=qCreatedBy(makeId("Front.planeOp"),FACE);
            mirror(context, id + "F8", {"entities" : qUnion([Q0]), "mirrorPlane" : qUnion([Q1])});
        }
    });
